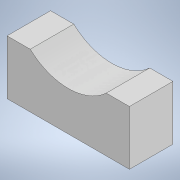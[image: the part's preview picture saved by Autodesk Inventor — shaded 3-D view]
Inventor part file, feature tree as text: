
AUTODESK INVENTOR PART (.ipt)
format: ipt  version: 2021 (Build 250183000, 183)  size: 139,264 bytes
history: native  units: in
note: dims shown in document units (in); Inventor stores cm internally (conversion verified against a paired STEP export)
features: extrude x2, sketch x2
ambient origin geometry x8: Origin, YZ Plane, XZ Plane, XY Plane, X Axis, Y Axis, Z Axis, Center Point
bodies: Solid1 (feature_tree)
feature tree (4):
  extrude  "Extrusion1"  Depth=20.0in
  extrude  "Extrusion3"  Depth=16.0in TaperAngle=0.0deg
  sketch  "Sketch1"  dims[d0=45.0in d1=20.0in]
  sketch  "Sketch4"  dims[d4=41.0in d5=16.0in d6=0.0in d13=12.2503in d14=6.5in d15=10.625in d16=2.6875in d17=0.625in d18=0.0in]
